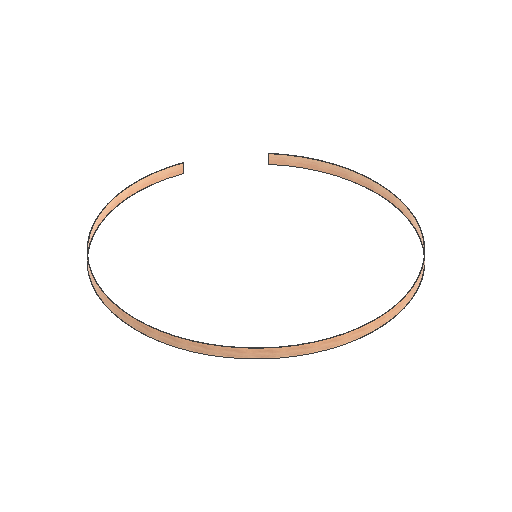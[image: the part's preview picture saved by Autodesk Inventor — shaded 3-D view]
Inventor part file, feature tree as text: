
AUTODESK INVENTOR PART (.ipt)
format: ipt  version: 2021 (Build 250183000, 183)  size: 114,688 bytes
history: native  units: mm
features: other x4, extrude x2, sketch x2, reference x2
ambient origin geometry x8: Origin, YZ Plane, XZ Plane, XY Plane, X Axis, Y Axis, Z Axis, Center Point
bodies: Solid1 (feature_tree)
feature tree (10):
  extrude  "Extrusion1"  Depth=2558.0mm
  extrude  "Extrusion2"  Depth=100.0mm TaperAngle=0.0deg
  sketch  "Sketch1"  dims[d0=2550.0mm d1=2558.0mm]
  sketch  "Sketch2"  dims[d2=100.0mm d3=0.0mm d4=100.0mm d5=0.0mm]
  reference  "Reference1"
  reference  "Reference2"
  other  "Full Scale Assembly.iam"
  other  "Disk D Assembly:1"
  other  "Platform D1:1"
  other  "Platform D4:1"
